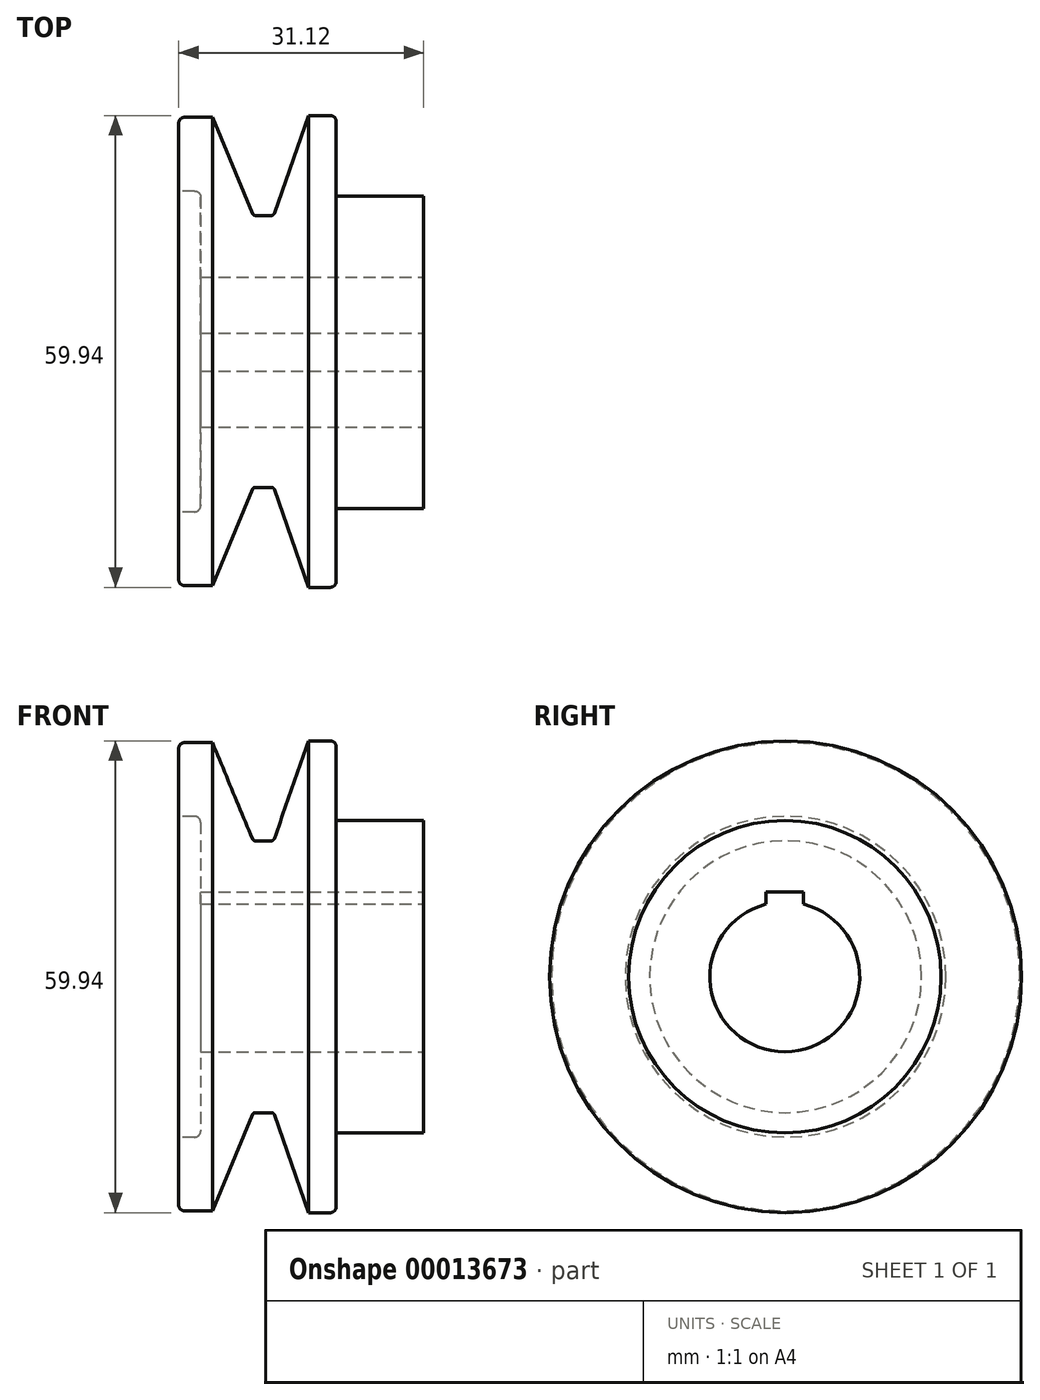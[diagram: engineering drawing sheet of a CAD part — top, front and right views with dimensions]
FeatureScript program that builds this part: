
annotation { "Feature Type Name" : "Feature", "Feature Type Description" : "" }
export const myFeature = defineFeature(function(context is Context, id is Id, definition is map)
    precondition{}
    {
        {
            var Q0;
            Q0=qCreatedBy(makeId("Top.planeOp"),FACE);
            var sketch = newSketch(context, id + "F0", { "sketchPlane" : qUnion([Q0])});
            skLineSegment(sketch, "E0", {"start": v(-3.62, 20.48) * mm, "end": v(-3.62, 29.09) * mm});
            skLineSegment(sketch, "E1", {"start": v(-2.86, 29.85) * mm, "end": v(0.66, 29.85) * mm});
            skLineSegment(sketch, "E2", {"start": v(0.66, 29.85) * mm, "end": v(5.74, 17.62) * mm});
            skArc(sketch, "E3.filletArc", {"start": v(-2.86, 29.85) * mm, "mid": v(-3.4, 29.62) * mm, "end": v(-3.62, 29.09) * mm});
            skLineSegment(sketch, "E4.0.MirrorCS", {"start": v(16.38, 0.1) * mm, "end": v(16.38, 29.31) * mm});
            skLineSegment(sketch, "E5", {"start": v(12.86, 30.07) * mm, "end": v(15.62, 30.07) * mm});
            skArc(sketch, "E6.filletArc", {"start": v(16.38, 29.31) * mm, "mid": v(16.16, 29.85) * mm, "end": v(15.62, 30.07) * mm});
            skLineSegment(sketch, "E7.0", {"start": v(-0.84, 0.1) * mm, "end": v(-0.84, 19.72) * mm});
            skLineSegment(sketch, "E8", {"start": v(-0.84, 0.1) * mm, "end": v(16.38, 0.1) * mm});
            skLineSegment(sketch, "E9.0.MirrorCS", {"start": v(12.86, 30.07) * mm, "end": v(8.53, 17.64) * mm});
            skLineSegment(sketch, "E10.0", {"start": v(6.1, 17.37) * mm, "end": v(8.16, 17.37) * mm});
            skLineSegment(sketch, "E11", {"start": v(-1.6, 20.48) * mm, "end": v(-3.62, 20.48) * mm});
            skPoint(sketch, "E12.visualSharp", {"position": v(-0.84, 20.48) * mm});
            skArc(sketch, "E12.filletArc", {"start": v(-0.84, 19.72) * mm, "mid": v(-1.06, 20.26) * mm, "end": v(-1.6, 20.48) * mm});
            skPoint(sketch, "E13.visualSharp", {"position": v(5.84, 17.37) * mm});
            skArc(sketch, "E13.filletArc", {"start": v(5.74, 17.62) * mm, "mid": v(5.89, 17.44) * mm, "end": v(6.1, 17.37) * mm});
            skPoint(sketch, "E14.visualSharp", {"position": v(8.44, 17.37) * mm});
            skArc(sketch, "E14.filletArc", {"start": v(8.16, 17.37) * mm, "mid": v(8.39, 17.45) * mm, "end": v(8.53, 17.64) * mm});
            skSolve(sketch);
        }
        {
            var Q0;
            Q0=makeQuery(id+"F0.imprint","IMPRINT",FACE,{"disambiguationData":[TD([[makeQuery(id+"F0.imprint","IMPRINT",EDGE,{"derivedFrom":sQuery(id+"F0.wireOp",EDGE,"E0")}),-1.0]])]});
            var Q1;
            Q1 = qSketchRegion(id + "F2", true);
            var Q2;
            Q2=sQuery(id+"F0.wireOp",EDGE,"E8");
            revolve(context, id + "F1", {"entities" : qUnion([Q0, Q1]), "axis" : qUnion([Q2]), "revolveType" : RevolveType.FULL});
        }
        {
            var Q0;
            Q0=makeQuery(id+"F1.opRevolve","SWEPT_FACE",FACE,{"disambiguationData":[OSD([sQuery(id+"F0.wireOp",EDGE,"E4.0.MirrorCS")])]});
            var sketch = newSketch(context, id + "F2", { "sketchPlane" : qUnion([Q0])});
            skCircle(sketch, "E15", {"center": v(0, 0) * mm, "radius": 19.84 * mm});
            skSolve(sketch);
        }
        {
            var Q0;
            Q0=makeQuery(id+"F2.imprint","IMPRINT",FACE,{"disambiguationData":[TD([[makeQuery(id+"F2.imprint","IMPRINT",EDGE,{"derivedFrom":sQuery(id+"F2.wireOp",EDGE,"E15")}),1.0]])]});
            extrude(context, id + "F3", {"entities" : qUnion([Q0]), "operationType" : NewBodyOperationType.ADD, "depth" : 11.1 * mm});
        }
        {
            var Q0;
            Q0=makeQuery(id+"F3.opExtrude","CAP_FACE",FACE,{"disambiguationData":[OSD([sQuery(id+"F2.wireOp",EDGE,"E15")])],"isStart":false});
            var sketch = newSketch(context, id + "F4", { "sketchPlane" : qUnion([Q0])});
            skArc(sketch, "E16", {"start": v(-2.4, 9.22) * mm, "mid": v(0, -9.53) * mm, "end": v(2.4, 9.22) * mm});
            skLineSegment(sketch, "E17.rect.bottom", {"start": v(2.4, 10.79) * mm, "end": v(-2.4, 10.79) * mm});
            skLineSegment(sketch, "E17.rect.left", {"start": v(2.4, 10.79) * mm, "end": v(2.4, 9.22) * mm});
            skLineSegment(sketch, "E17.rect.right", {"start": v(-2.4, 10.79) * mm, "end": v(-2.4, 9.22) * mm});
            skSolve(sketch);
        }
        {
            var Q0;
            Q0=makeQuery(id+"F4.imprint","IMPRINT",FACE,{"disambiguationData":[TD([[makeQuery(id+"F4.imprint","IMPRINT",EDGE,{"derivedFrom":sQuery(id+"F4.wireOp",EDGE,"E16")}),1.0]])]});
            extrude(context, id + "F5", {"entities" : qUnion([Q0]), "operationType" : NewBodyOperationType.REMOVE, "oppositeDirection" : true, "depth" : 115.94 * mm});
        }
    });
